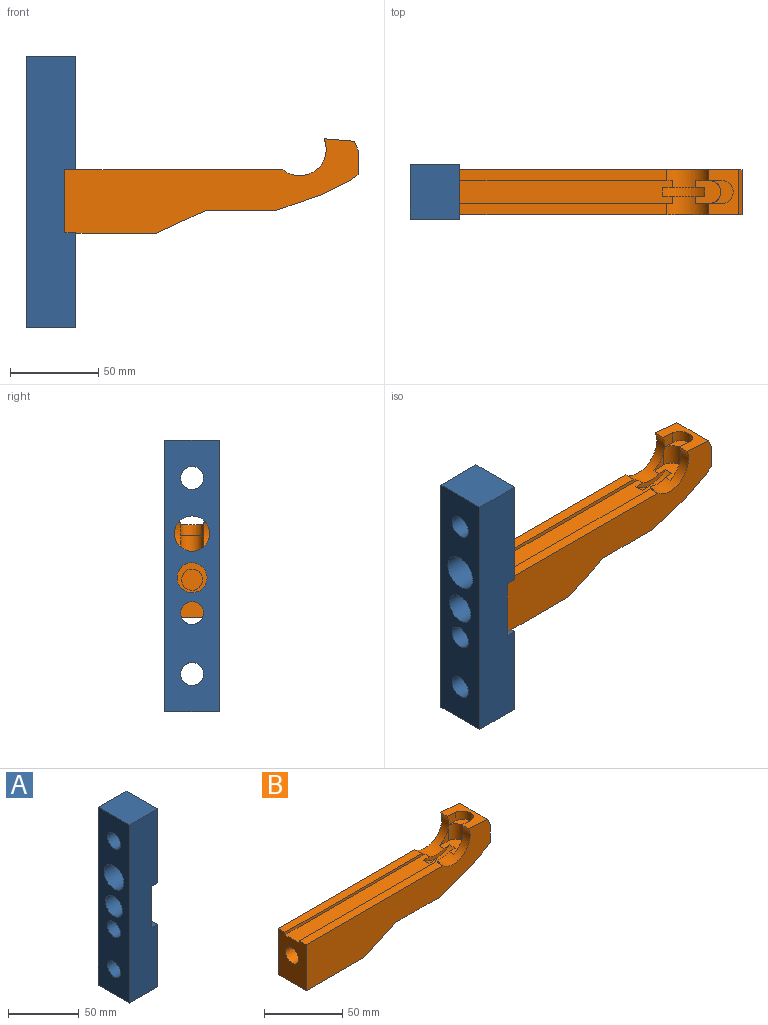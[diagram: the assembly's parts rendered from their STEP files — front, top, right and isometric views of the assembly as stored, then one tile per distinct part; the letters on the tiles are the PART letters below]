
ASSEMBLY  parts=2 mates=1
PART A: 16 faces, bbox 28x31x154 mm
  f0: plane 9.32x6mm, normal (0,0,1), area 55.9mm2, adj f1,f3,f9,f13
  f1: plane 54x31mm, normal (1,0,0), area 1500.5mm2, adj f0,f2,f8,f9,f10,f13,f15
  f2: plane 9.32x6mm, normal (0,0,1), area 55.9mm2, adj f1,f3,f10,f13
  f3: plane 36x31mm, normal (1,0,0), area 797.1mm2, adj f0,f2,f4,f9,f10,f13,f14
  f4: plane 31x6mm, normal (0,0,-1), area 186mm2, adj f3,f5,f9,f10
  f5: plane 64x31mm, normal (1,0,0), area 1537.1mm2, adj f4,f6,f9,f10,f11,f12
  f6: plane 31x28mm, normal (0,0,1), area 868mm2, adj f5,f7,f9,f10
  f7: plane 154x31mm, normal (-1,0,0), area 3834.7mm2, adj f6,f8,f9,f10,f11,f12,f13,f14
  f8: plane 31x28mm, normal (0,0,-1), area 868mm2, adj f1,f7,f9,f10
  f9: plane 154x28mm, normal (0,-1,0), area 4096mm2, adj f0,f1,f3,f4,f5,f6,f7,f8
  f10: plane 154x28mm, normal (0,1,0), area 4096mm2, adj f1,f2,f3,f4,f5,f6,f7,f8
  f11: cylinder r=10mm len=28mm, axis (-1,0,0), area 1759.3mm2, adj f5,f7
  f12: cylinder r=6.5mm len=28mm, axis (-1,0,0), area 1143.5mm2, adj f5,f7
  f13: cylinder r=6.5mm len=28mm, axis (-1,0,0), area 996.6mm2, adj f0,f1,f2,f3,f7
  f14: cylinder r=8.5mm len=22mm, axis (-1,0,0), area 1175mm2, adj f3,f7
  f15: cylinder r=6.5mm len=28mm, axis (-1,0,0), area 1143.5mm2, adj f1,f7
PART B: 32 faces, bbox 166x25.5x53.4 mm
  f0: cylinder r=15mm len=24.63mm, axis (0,1,0), area 304.9mm2, adj f1,f2,f4,f6,f19,f20,f21,f24
  f1: plane 25.5x17.22mm, normal (0.08,0,1), area 273.4mm2, adj f0,f8,f17,f18,f19,f25,f26,f28
  f2: cylinder r=6.5mm len=13mm, axis (0,0,-1), area 243.9mm2, adj f0,f8,f23,f24,f27,f29
  f3: cylinder r=18mm len=23.81mm, axis (0,-1,0), area 130.1mm2, adj f4,f5,f20,f27
  f4: plane 23.81x4.5mm, normal (0,-1,0), area 60.2mm2, adj f0,f3,f20,f27
  f5: plane 23.81x4.5mm, normal (0,1,0), area 60.2mm2, adj f3,f8,f20,f27
  f6: plane 123.37x6.25mm, normal (0,0,1), area 771.1mm2, adj f0,f7,f19,f21
  f7: plane 36x25.5mm, normal (-1,0,0), area 778.9mm2, adj f6,f9,f10,f18,f19,f20,f21,f22
  f8: cylinder r=15mm len=24.63mm, axis (0,1,0), area 304.9mm2, adj f1,f2,f5,f9,f18,f20,f22,f23
  f9: plane 123.37x6.25mm, normal (0,0,1), area 771.1mm2, adj f7,f8,f18,f22
  f10: plane 52x25.5mm, normal (0,0,-1), area 1326mm2, adj f7,f11,f18,f19
  f11: plane 28x25.5mm, normal (0.42,0,-0.91), area 787.2mm2, adj f10,f12,f18,f19
  f12: plane 40x25.5mm, normal (0,0,-1), area 1020mm2, adj f11,f13,f18,f19
  f13: plane 26x25.5mm, normal (0.33,0,-0.94), area 701.6mm2, adj f12,f14,f18,f19
  f14: plane 25.5x16mm, normal (0.45,0,-0.89), area 456.2mm2, adj f13,f15,f18,f19
  f15: plane 25.5x4mm, normal (0.6,0,-0.8), area 127.5mm2, adj f14,f16,f18,f19
  f16: plane 25.5x14mm, normal (1,0,0), area 357mm2, adj f15,f17,f18,f19
  f17: plane 25.5x5mm, normal (0.93,0,0.37), area 137.3mm2, adj f1,f16,f18,f19
  f18: plane 166x53.44mm, normal (0,-1,0), area 4545.7mm2, adj f1,f7,f8,f9,f10,f11,f12,f13
  f19: plane 166x53.44mm, normal (0,1,0), area 4545.7mm2, adj f0,f1,f6,f7,f10,f11,f12,f13
  f20: plane 126.46x13mm, normal (0,0,1), area 1617.2mm2, adj f0,f3,f4,f5,f7,f8,f21,f22
  f21: plane 126.46x2mm, normal (0,-1,0), area 249.6mm2, adj f0,f6,f7,f20
  f22: plane 126.46x2mm, normal (0,1,0), area 249.6mm2, adj f7,f8,f9,f20
  f23: plane 9.66x7.96mm, normal (0,1,0), area 26.9mm2, adj f2,f8,f27
  f24: plane 9.66x7.96mm, normal (0,-1,0), area 26.9mm2, adj f0,f2,f27
  f25: plane 7.72x7.44mm, normal (0,1,0), area 48.3mm2, adj f1,f8,f28,f29
  f26: plane 7.72x7.44mm, normal (0,-1,0), area 48.3mm2, adj f0,f1,f28,f29
  f27: plane 14.46x13mm, normal (0,0,1), area 143mm2, adj f0,f2,f3,f4,f5,f8,f23,f24
  f28: cylinder r=6.5mm len=13mm, axis (0,0,-1), area 131.6mm2, adj f1,f25,f26,f29
  f29: plane 13.08x13mm, normal (0,0,1), area 91mm2, adj f0,f2,f8,f25,f26,f28
  f30: cylinder r=6mm len=30mm, axis (-1,0,0), area 1131mm2, adj f7,f31
  f31: plane 12x12mm, normal (-1,0,0), area 113.1mm2, adj f30
PLACE A t=(81.98,29.2,-7.31)mm
PLACE B t=(89.98,29.14,-30.62)mm
MATE planar A.f3 <-> B.f7  axis (1,0,0) through (89.98,29.2,5.69)mm
